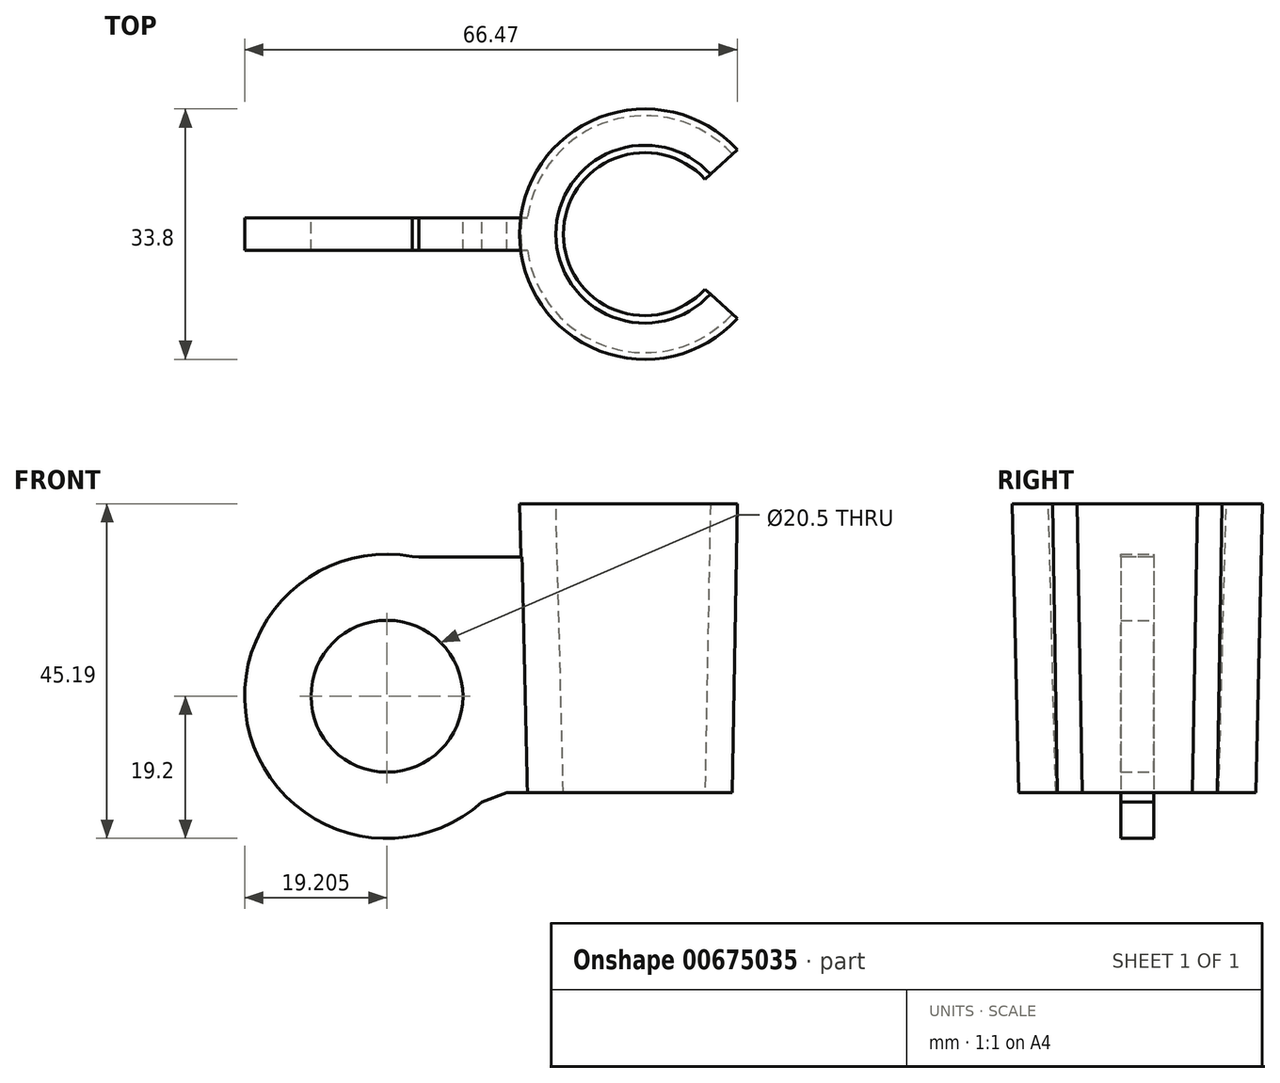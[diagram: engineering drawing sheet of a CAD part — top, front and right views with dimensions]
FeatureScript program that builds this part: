
annotation { "Feature Type Name" : "Feature", "Feature Type Description" : "" }
export const myFeature = defineFeature(function(context is Context, id is Id, definition is map)
    precondition{}
    {
        {
            var Q0;
            Q0=qCreatedBy(makeId("Top.planeOp"),FACE);
            var sketch = newSketch(context, id + "F0", { "sketchPlane" : qUnion([Q0])});
            skCircle(sketch, "E0", {"center": v(0, 0) * mm, "radius": 11 * mm});
            skCircle(sketch, "E1", {"center": v(0, 0) * mm, "radius": 12 * mm});
            skSolve(sketch);
        }
        {
            var Q0;
            Q0=qCreatedBy(makeId("Front.planeOp"),FACE);
            var sketch = newSketch(context, id + "F1", { "sketchPlane" : qUnion([Q0])});
            skLineSegment(sketch, "E2", {"start": v(-11, 0) * mm, "end": v(0, 0) * mm});
            skLineSegment(sketch, "E3", {"start": v(0, 38.99) * mm, "end": v(-12, 38.99) * mm});
            skLineSegment(sketch, "E4", {"start": v(-12, 38.99) * mm, "end": v(-11, 0) * mm});
            skLineSegment(sketch, "E5", {"start": v(0, 38.99) * mm, "end": v(0, 43.99) * mm});
            skLineSegment(sketch, "E6", {"start": v(0, 43.99) * mm, "end": v(-17.02, 43.99) * mm});
            skLineSegment(sketch, "E7", {"start": v(-17.02, 43.99) * mm, "end": v(-16, 0) * mm});
            skLineSegment(sketch, "E8", {"start": v(-16, 0) * mm, "end": v(-11, 0) * mm});
            skLineSegment(sketch, "E9", {"start": v(-12, 38.99) * mm, "end": v(-12.18, 46.64) * mm});
            skLineSegment(sketch, "E10", {"start": v(-12, 38.99) * mm, "end": v(-23.93, 38.99) * mm});
            skSolve(sketch);
        }
        {
            var Q0;
            {var subQ4=sQuery(id+"F1.wireOp",EDGE,"E4");Q0=makeQuery(id+"F1.imprint","IMPRINT",FACE,{"disambiguationData":[TD([[makeQuery(id+"F1.imprint","IMPRINT",EDGE,{"derivedFrom":subQ4}),-1.0]])]});}
            var Q1;
            Q1=sQuery(id+"F0.wireOp",EDGE,"E1");
            revolve(context, id + "F2", {"entities" : qUnion([Q0]), "axis" : qUnion([Q1]), "revolveType" : RevolveType.SYMMETRIC, "angle" : 275 * degree});
        }
        {
            var Q0;
            Q0=qCreatedBy(makeId("Front.planeOp"),FACE);
            var sketch = newSketch(context, id + "F3", { "sketchPlane" : qUnion([Q0])});
            skCircle(sketch, "E11", {"center": v(-34.8, 13) * mm, "radius": 19.2 * mm});
            skLineSegment(sketch, "E12", {"start": v(17.88, 39) * mm, "end": v(-28.18, 39) * mm});
            skLineSegment(sketch, "E13", {"start": v(20.65, 0) * mm, "end": v(-33.45, 0) * mm});
            skCircle(sketch, "E14", {"center": v(-34.8, 13) * mm, "radius": 10.25 * mm});
            skLineSegment(sketch, "E15", {"start": v(-30.98, 31.82) * mm, "end": v(-15.41, 31.82) * mm});
            skLineSegment(sketch, "E16", {"start": v(-15.41, 31.82) * mm, "end": v(-15.41, 0) * mm});
            skLineSegment(sketch, "E17", {"start": v(-15.41, 0) * mm, "end": v(-20.68, 0) * mm});
            skSolve(sketch);
        }
        {
            var Q0;
            Q0 = qSketchRegion(id + "F3", true);
            extrude(context, id + "F4", {"entities" : qUnion([Q0]), "operationType" : NewBodyOperationType.ADD, "endBound" : BoundingType.SYMMETRIC, "depth" : 4.4 * mm, "offsetDistance" : 25 * mm});
        }
        {
            var Q0;
            Q0=makeQuery(id+"F4.opExtrude","SWEPT_EDGE",EDGE,{"disambiguationData":[OSD([sQuery(id+"F3.wireOp",EDGE,"E11"),sQuery(id+"F3.wireOp",EDGE,"E17")])]});
            chamfer(context, id + "F5", {"entities" : qUnion([Q0]), "width" : 5 * mm, "tangentPropagation" : true});
        }
    });
